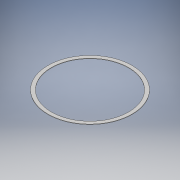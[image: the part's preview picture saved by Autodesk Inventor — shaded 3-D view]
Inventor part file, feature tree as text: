
AUTODESK INVENTOR PART (.ipt)
format: ipt  version: 2017 (Build 210142000, 142)  size: 103,424 bytes
history: native  units: in
note: dims shown in document units (in); Inventor stores cm internally (conversion verified against a paired STEP export)
features: extrude x1, sketch x1
ambient origin geometry x8: Origin, YZ Plane, XZ Plane, XY Plane, X Axis, Y Axis, Z Axis, Center Point
bodies: Solid1 (feature_tree)
feature tree (2):
  extrude  "Extrusion1"  Depth=0.0625in
  sketch  "Sketch1"  dims[d0=11.9713in d1=10.989in d2=0.0625in d3=0.0in]
